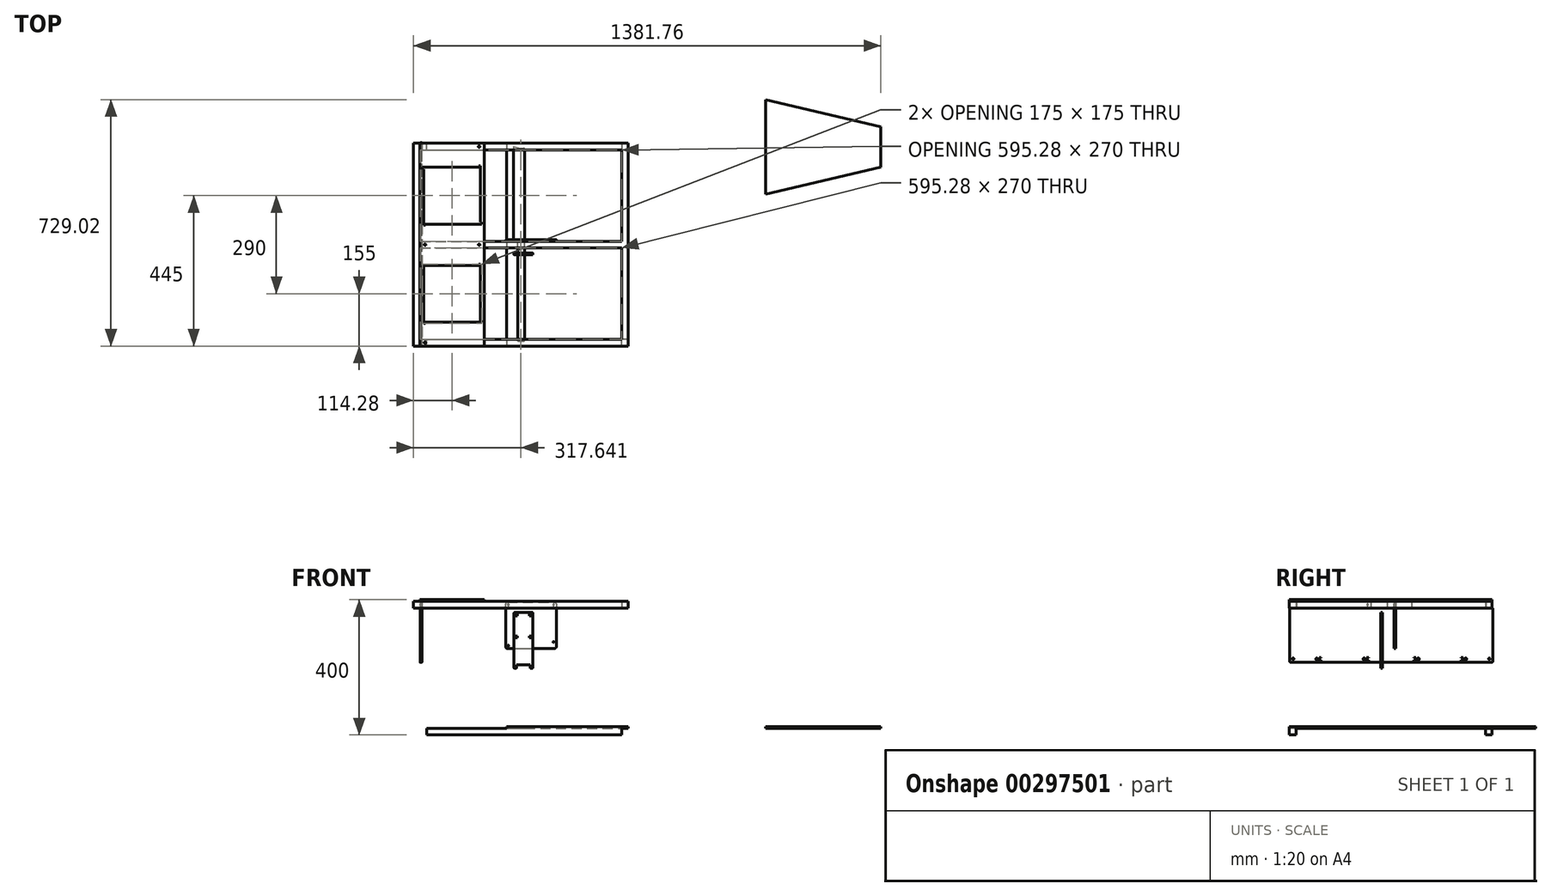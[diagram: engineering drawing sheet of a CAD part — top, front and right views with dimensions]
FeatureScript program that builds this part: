
annotation { "Feature Type Name" : "Feature", "Feature Type Description" : "" }
export const myFeature = defineFeature(function(context is Context, id is Id, definition is map)
    precondition{}
    {
        {
            var Q0;
            Q0=qCreatedBy(makeId("Front.planeOp"),FACE);
            var sketch = newSketch(context, id + "F0", { "sketchPlane" : qUnion([Q0])});
            skLineSegment(sketch, "E0", {"start": v(-53, 64) * mm, "end": v(-53, 191) * mm});
            skCircle(sketch, "E1", {"center": v(-45, 67) * mm, "radius": 1.4 * mm});
            skCircle(sketch, "E2", {"center": v(89, 78) * mm, "radius": 1.4 * mm});
            skLineSegment(sketch, "E3", {"start": v(97, 191) * mm, "end": v(97, 64) * mm});
            skLineSegment(sketch, "E4", {"start": v(-48, 196) * mm, "end": v(92, 196) * mm});
            skArc(sketch, "E5.filletArc", {"start": v(-48, 196) * mm, "mid": v(-51.54, 194.54) * mm, "end": v(-53, 191) * mm});
            skArc(sketch, "E6.filletArc", {"start": v(97, 191) * mm, "mid": v(95.54, 194.54) * mm, "end": v(92, 196) * mm});
            skCircle(sketch, "E7", {"center": v(-45, 188) * mm, "radius": 2.25 * mm});
            skCircle(sketch, "E8", {"center": v(89, 188) * mm, "radius": 2.25 * mm});
            skLineSegment(sketch, "E9", {"start": v(-48, 59) * mm, "end": v(92, 59) * mm});
            skArc(sketch, "E10.filletArc", {"start": v(-53, 64) * mm, "mid": v(-51.54, 60.46) * mm, "end": v(-48, 59) * mm});
            skArc(sketch, "E11.filletArc", {"start": v(92, 59) * mm, "mid": v(95.54, 60.46) * mm, "end": v(97, 64) * mm});
            skPoint(sketch, "E12", {"position": v(0, 0) * mm});
            skLineSegment(sketch, "E13.bottom", {"start": v(-23.05, 160.05) * mm, "end": v(-17.95, 160.05) * mm});
            skLineSegment(sketch, "E13.top", {"start": v(-23.05, 154.95) * mm, "end": v(-17.95, 154.95) * mm});
            skLineSegment(sketch, "E13.left", {"start": v(-23.05, 160.05) * mm, "end": v(-23.05, 154.95) * mm});
            skLineSegment(sketch, "E13.right", {"start": v(-17.95, 160.05) * mm, "end": v(-17.95, 154.95) * mm});
            skLineSegment(sketch, "E14.bottom", {"start": v(17.95, 160.05) * mm, "end": v(23.05, 160.05) * mm});
            skLineSegment(sketch, "E14.top", {"start": v(17.95, 154.95) * mm, "end": v(23.05, 154.95) * mm});
            skLineSegment(sketch, "E14.left", {"start": v(17.95, 160.05) * mm, "end": v(17.95, 154.95) * mm});
            skLineSegment(sketch, "E14.right", {"start": v(23.05, 160.05) * mm, "end": v(23.05, 154.95) * mm});
            skLineSegment(sketch, "E15.bottom", {"start": v(-23.05, 95.05) * mm, "end": v(-17.95, 95.05) * mm});
            skLineSegment(sketch, "E15.top", {"start": v(-23.05, 89.95) * mm, "end": v(-17.95, 89.95) * mm});
            skLineSegment(sketch, "E15.left", {"start": v(-23.05, 95.05) * mm, "end": v(-23.05, 89.95) * mm});
            skLineSegment(sketch, "E15.right", {"start": v(-17.95, 95.05) * mm, "end": v(-17.95, 89.95) * mm});
            skLineSegment(sketch, "E16.bottom", {"start": v(23.05, 95.05) * mm, "end": v(17.95, 95.05) * mm});
            skLineSegment(sketch, "E16.top", {"start": v(23.05, 89.95) * mm, "end": v(17.95, 89.95) * mm});
            skLineSegment(sketch, "E16.left", {"start": v(23.05, 95.05) * mm, "end": v(23.05, 89.95) * mm});
            skLineSegment(sketch, "E16.right", {"start": v(17.95, 95.05) * mm, "end": v(17.95, 89.95) * mm});
            skPoint(sketch, "E17", {"position": v(-20.5, 160.05) * mm});
            skPoint(sketch, "E18", {"position": v(20.5, 160.05) * mm});
            skPoint(sketch, "E19", {"position": v(23.05, 157.5) * mm});
            skPoint(sketch, "E20", {"position": v(-23.05, 157.5) * mm});
            skPoint(sketch, "E21", {"position": v(-23.05, 92.5) * mm});
            skPoint(sketch, "E22", {"position": v(17.95, 92.5) * mm});
            skPoint(sketch, "E23.middle.positionSnap0", {"position": v(23.05, 92.5) * mm});
            skPoint(sketch, "E23.centerSnap0", {"position": v(23.05, 92.5) * mm});
            skPoint(sketch, "E24", {"position": v(60.49, 176) * mm});
            skSolve(sketch);
        }
        {
            var Q0;
            Q0=qCreatedBy(makeId("Front.planeOp"),FACE);
            cPlane(context, id + "F1", {"entities" : qUnion([Q0]), "cplaneType" : CPlaneType.OFFSET, "offset" : (17 + 18) * mm, "width" : 150 * mm, "height" : 150 * mm});
        }
        {
            var Q0;
            Q0=qCreatedBy(id+"F1.planeOp",FACE);
            var sketch = newSketch(context, id + "F2", { "sketchPlane" : qUnion([Q0])});
            skPoint(sketch, "E25", {"position": v(0, 0) * mm});
            skCircle(sketch, "E26", {"center": v(-24, 5) * mm, "radius": 1.4 * mm});
            skCircle(sketch, "E27", {"center": v(24, 5) * mm, "radius": 1.4 * mm});
            skLineSegment(sketch, "E28", {"start": v(-26, 0) * mm, "end": v(-22, 0) * mm});
            skLineSegment(sketch, "E29.trimOffspring", {"start": v(22, 0) * mm, "end": v(26, 0) * mm});
            skLineSegment(sketch, "E30.top", {"start": v(-20, 11) * mm, "end": v(20, 11) * mm});
            skLineSegment(sketch, "E30.left", {"start": v(-20, 2) * mm, "end": v(-20, 11) * mm});
            skLineSegment(sketch, "E30.right", {"start": v(20, 2) * mm, "end": v(20, 11) * mm});
            skPoint(sketch, "E30.middle", {"position": v(0, 5.5) * mm});
            skLineSegment(sketch, "E31", {"start": v(-28, 2) * mm, "end": v(-28, 163) * mm});
            skLineSegment(sketch, "E32", {"start": v(-26, 165) * mm, "end": v(26, 165) * mm});
            skLineSegment(sketch, "E33", {"start": v(28, 163) * mm, "end": v(28, 2) * mm});
            skLineSegment(sketch, "E34.bottom", {"start": v(-23.05, 160.05) * mm, "end": v(-17.95, 160.05) * mm});
            skLineSegment(sketch, "E34.top", {"start": v(-23.05, 154.95) * mm, "end": v(-17.95, 154.95) * mm});
            skLineSegment(sketch, "E34.left", {"start": v(-23.05, 160.05) * mm, "end": v(-23.05, 154.95) * mm});
            skLineSegment(sketch, "E34.right", {"start": v(-17.95, 160.05) * mm, "end": v(-17.95, 154.95) * mm});
            skLineSegment(sketch, "E35.bottom", {"start": v(17.95, 160.05) * mm, "end": v(23.05, 160.05) * mm});
            skLineSegment(sketch, "E35.top", {"start": v(17.95, 154.95) * mm, "end": v(23.05, 154.95) * mm});
            skLineSegment(sketch, "E35.left", {"start": v(17.95, 160.05) * mm, "end": v(17.95, 154.95) * mm});
            skLineSegment(sketch, "E35.right", {"start": v(23.05, 160.05) * mm, "end": v(23.05, 154.95) * mm});
            skLineSegment(sketch, "E36.bottom", {"start": v(-23.05, 95.05) * mm, "end": v(-17.95, 95.05) * mm});
            skLineSegment(sketch, "E36.top", {"start": v(-23.05, 89.95) * mm, "end": v(-17.95, 89.95) * mm});
            skLineSegment(sketch, "E36.left", {"start": v(-23.05, 95.05) * mm, "end": v(-23.05, 89.95) * mm});
            skLineSegment(sketch, "E36.right", {"start": v(-17.95, 95.05) * mm, "end": v(-17.95, 89.95) * mm});
            skLineSegment(sketch, "E37.bottom", {"start": v(23.05, 95.05) * mm, "end": v(17.95, 95.05) * mm});
            skLineSegment(sketch, "E37.top", {"start": v(23.05, 89.95) * mm, "end": v(17.95, 89.95) * mm});
            skLineSegment(sketch, "E37.left", {"start": v(23.05, 95.05) * mm, "end": v(23.05, 89.95) * mm});
            skLineSegment(sketch, "E37.right", {"start": v(17.95, 95.05) * mm, "end": v(17.95, 89.95) * mm});
            skPoint(sketch, "E38.visualSharp", {"position": v(-28, 0) * mm});
            skArc(sketch, "E38.filletArc", {"start": v(-28, 2) * mm, "mid": v(-27.41, 0.59) * mm, "end": v(-26, 0) * mm});
            skPoint(sketch, "E39.visualSharp", {"position": v(-20, 0) * mm});
            skArc(sketch, "E39.filletArc", {"start": v(-22, 0) * mm, "mid": v(-20.59, 0.59) * mm, "end": v(-20, 2) * mm});
            skPoint(sketch, "E40.visualSharp", {"position": v(20, 0) * mm});
            skArc(sketch, "E40.filletArc", {"start": v(20, 2) * mm, "mid": v(20.59, 0.59) * mm, "end": v(22, 0) * mm});
            skPoint(sketch, "E41.visualSharp", {"position": v(28, 0) * mm});
            skArc(sketch, "E41.filletArc", {"start": v(26, 0) * mm, "mid": v(27.41, 0.59) * mm, "end": v(28, 2) * mm});
            skPoint(sketch, "E42.visualSharp", {"position": v(-28, 165) * mm});
            skArc(sketch, "E42.filletArc", {"start": v(-26, 165) * mm, "mid": v(-27.41, 164.41) * mm, "end": v(-28, 163) * mm});
            skPoint(sketch, "E43.visualSharp", {"position": v(28, 165) * mm});
            skArc(sketch, "E43.filletArc", {"start": v(28, 163) * mm, "mid": v(27.41, 164.41) * mm, "end": v(26, 165) * mm});
            skPoint(sketch, "E44", {"position": v(-20.5, 160.05) * mm});
            skPoint(sketch, "E45", {"position": v(20.5, 160.05) * mm});
            skPoint(sketch, "E46", {"position": v(23.05, 157.5) * mm});
            skPoint(sketch, "E47", {"position": v(-23.05, 157.5) * mm});
            skPoint(sketch, "E48", {"position": v(-23.05, 92.5) * mm});
            skPoint(sketch, "E49", {"position": v(17.95, 92.5) * mm});
            skLineSegment(sketch, "E50", {"start": v(38, 165) * mm, "end": v(38, 160) * mm});
            skLineSegment(sketch, "E51.bottom", {"start": v(38, 155) * mm, "end": v(33, 155) * mm});
            skLineSegment(sketch, "E51.top", {"start": v(38, 160) * mm, "end": v(33, 160) * mm});
            skLineSegment(sketch, "E51.right", {"start": v(33, 155) * mm, "end": v(33, 160) * mm});
            skPoint(sketch, "E51.middle", {"position": v(35.5, 157.5) * mm});
            skLineSegment(sketch, "E52.bottom", {"start": v(38, 90) * mm, "end": v(33, 90) * mm});
            skLineSegment(sketch, "E52.top", {"start": v(38, 95) * mm, "end": v(33, 95) * mm});
            skLineSegment(sketch, "E52.right", {"start": v(33, 90) * mm, "end": v(33, 95) * mm});
            skPoint(sketch, "E52.middle", {"position": v(35.5, 92.5) * mm});
            skPoint(sketch, "E52.middle.positionSnap0", {"position": v(23.05, 92.5) * mm});
            skPoint(sketch, "E52.centerSnap0", {"position": v(23.05, 92.5) * mm});
            skLineSegment(sketch, "E53.bottom", {"start": v(-40, 160) * mm, "end": v(-35, 160) * mm});
            skLineSegment(sketch, "E53.top", {"start": v(-40, 155) * mm, "end": v(-35, 155) * mm});
            skLineSegment(sketch, "E53.right", {"start": v(-35, 160) * mm, "end": v(-35, 155) * mm});
            skPoint(sketch, "E53.middle", {"position": v(-37.5, 157.5) * mm});
            skLineSegment(sketch, "E54.bottom", {"start": v(-40, 95) * mm, "end": v(-35, 95) * mm});
            skLineSegment(sketch, "E54.top", {"start": v(-40, 90) * mm, "end": v(-35, 90) * mm});
            skLineSegment(sketch, "E54.right", {"start": v(-35, 95) * mm, "end": v(-35, 90) * mm});
            skPoint(sketch, "E54.middle", {"position": v(-37.5, 92.5) * mm});
            skLineSegment(sketch, "E55.trimOffspring", {"start": v(38, 155) * mm, "end": v(38, 95) * mm});
            skLineSegment(sketch, "E56.trimOffspring", {"start": v(38, 90) * mm, "end": v(38, 85) * mm});
            skLineSegment(sketch, "E57", {"start": v(38, 165) * mm, "end": v(59, 165) * mm});
            skLineSegment(sketch, "E58", {"start": v(59, 165) * mm, "end": v(59, 160) * mm});
            skLineSegment(sketch, "E59", {"start": v(59, 160) * mm, "end": v(64, 160) * mm});
            skLineSegment(sketch, "E60", {"start": v(64, 160) * mm, "end": v(64, 155) * mm});
            skLineSegment(sketch, "E61", {"start": v(64, 155) * mm, "end": v(59, 155) * mm});
            skLineSegment(sketch, "E62", {"start": v(59, 155) * mm, "end": v(59, 95) * mm});
            skLineSegment(sketch, "E63", {"start": v(59, 95) * mm, "end": v(64, 95) * mm});
            skLineSegment(sketch, "E64", {"start": v(64, 95) * mm, "end": v(64, 90) * mm});
            skLineSegment(sketch, "E65", {"start": v(64, 90) * mm, "end": v(59, 90) * mm});
            skLineSegment(sketch, "E66", {"start": v(59, 90) * mm, "end": v(59, 85) * mm});
            skLineSegment(sketch, "E67", {"start": v(59, 85) * mm, "end": v(38, 85) * mm});
            skLineSegment(sketch, "E68.trimOffspring", {"start": v(-40, 155) * mm, "end": v(-40, 95) * mm});
            skPoint(sketch, "E69.start.orphan", {"position": v(-40, 165) * mm});
            skLineSegment(sketch, "E70.trimOffspring", {"start": v(-40, 90) * mm, "end": v(-40, 85) * mm});
            skLineSegment(sketch, "E71", {"start": v(-40, 160) * mm, "end": v(-40, 165) * mm});
            skLineSegment(sketch, "E72", {"start": v(-40, 165) * mm, "end": v(-61, 165) * mm});
            skLineSegment(sketch, "E73", {"start": v(-61, 165) * mm, "end": v(-61, 160) * mm});
            skLineSegment(sketch, "E74", {"start": v(-61, 160) * mm, "end": v(-66, 160) * mm});
            skLineSegment(sketch, "E75", {"start": v(-66, 160) * mm, "end": v(-66, 155) * mm});
            skPoint(sketch, "E75.endSnap0", {"position": v(-37.5, 155) * mm});
            skLineSegment(sketch, "E76", {"start": v(-66, 155) * mm, "end": v(-61, 155) * mm});
            skLineSegment(sketch, "E77", {"start": v(-61, 155) * mm, "end": v(-61, 95) * mm});
            skLineSegment(sketch, "E78", {"start": v(-61, 95) * mm, "end": v(-66, 95) * mm});
            skLineSegment(sketch, "E79", {"start": v(-66, 95) * mm, "end": v(-66, 90) * mm});
            skLineSegment(sketch, "E80", {"start": v(-66, 90) * mm, "end": v(-61, 90) * mm});
            skLineSegment(sketch, "E81", {"start": v(-61, 90) * mm, "end": v(-61, 85) * mm});
            skLineSegment(sketch, "E82", {"start": v(-61, 85) * mm, "end": v(-40, 85) * mm});
            skSolve(sketch);
        }
        {
            var Q0;
            Q0=makeQuery(id+"F2.imprint","IMPRINT",FACE,{"disambiguationData":[TD([[makeQuery(id+"F2.imprint","IMPRINT",EDGE,{"derivedFrom":sQuery(id+"F2.wireOp",EDGE,"E26")}),-1.0]])]});
            extrude(context, id + "F3", {"entities" : qUnion([Q0]), "depth" : 5 * mm});
        }
        {
            var Q0;
            Q0=makeQuery(id+"F0.imprint","IMPRINT",FACE,{"disambiguationData":[TD([[makeQuery(id+"F0.imprint","IMPRINT",EDGE,{"derivedFrom":sQuery(id+"F0.wireOp",EDGE,"E0")}),-1.0]])]});
            extrude(context, id + "F4", {"entities" : qUnion([Q0]), "oppositeDirection" : true, "depth" : 5 * mm});
        }
        {
            var Q0;
            Q0=qCreatedBy(id+"F1.planeOp",FACE);
            var sketch = newSketch(context, id + "F5", { "sketchPlane" : qUnion([Q0])});
            skPoint(sketch, "E83", {"position": v(-11.66, -156.67) * mm});
            skPoint(sketch, "E84", {"position": v(-265.28, 29.4) * mm});
            skPoint(sketch, "E85", {"position": v(168.31, 153.68) * mm});
            skLineSegment(sketch, "E86.bottom", {"start": v(-17.16, -156.67) * mm, "end": v(3.84, -156.67) * mm});
            skLineSegment(sketch, "E86.top", {"start": v(-17.16, -151.67) * mm, "end": v(3.84, -151.67) * mm});
            skLineSegment(sketch, "E86.left", {"start": v(-17.16, -156.67) * mm, "end": v(-17.16, -151.67) * mm});
            skLineSegment(sketch, "E86.right", {"start": v(3.84, -156.67) * mm, "end": v(3.84, -151.67) * mm});
            skCircle(sketch, "E87", {"center": v(168.31, 153.68) * mm, "radius": 6 * mm});
            skSolve(sketch);
        }
        {
            var Q0;
            Q0=qCreatedBy(makeId("Top.planeOp"),FACE);
            cPlane(context, id + "F6", {"entities" : qUnion([Q0]), "cplaneType" : CPlaneType.OFFSET, "offset" : 172 * mm, "oppositeDirection" : true, "width" : 150 * mm, "height" : 150 * mm});
        }
        {
            var Q0;
            Q0=qCreatedBy(id+"F6.planeOp",FACE);
            var sketch = newSketch(context, id + "F7", { "sketchPlane" : qUnion([Q0])});
            skLineSegment(sketch, "E88.top", {"start": v(290, 290) * mm, "end": v(-50, 290) * mm});
            skLineSegment(sketch, "E89.top", {"start": v(290, -310) * mm, "end": v(-50, -310) * mm});
            skLineSegment(sketch, "E90", {"start": v(-50, 290) * mm, "end": v(-50, -310) * mm});
            skLineSegment(sketch, "E91", {"start": v(310, 269.5) * mm, "end": v(310, -289.5) * mm});
            skPoint(sketch, "E92", {"position": v(310, -10) * mm});
            skLineSegment(sketch, "E93.top", {"start": v(310, 269.5) * mm, "end": v(290, 269.5) * mm});
            skLineSegment(sketch, "E93.right", {"start": v(290, 290) * mm, "end": v(290, 269.5) * mm});
            skPoint(sketch, "E93.left.start.orphan", {"position": v(310, 290) * mm});
            skLineSegment(sketch, "E94.top", {"start": v(310, -289.5) * mm, "end": v(290, -289.5) * mm});
            skLineSegment(sketch, "E94.right", {"start": v(290, -310) * mm, "end": v(290, -289.5) * mm});
            skPoint(sketch, "E94.left.start.orphan", {"position": v(310, -310) * mm});
            skLineSegment(sketch, "E95", {"start": v(-30, 280) * mm, "end": v(-30, 0) * mm});
            skLineSegment(sketch, "E96", {"start": v(310, 200) * mm, "end": v(310, 80) * mm});
            skLineSegment(sketch, "E97", {"start": v(-30, 280) * mm, "end": v(310, 200) * mm});
            skLineSegment(sketch, "E98", {"start": v(-30, 0) * mm, "end": v(310, 80) * mm});
            skPoint(sketch, "E99.middle", {"position": v(-11.66, -35) * mm});
            skLineSegment(sketch, "E100", {"start": v(-17.16, -54.99) * mm, "end": v(-17.16, 17.36) * mm});
            skLineSegment(sketch, "E101", {"start": v(3.84, 16.76) * mm, "end": v(3.84, -54.7) * mm});
            skPoint(sketch, "E102", {"position": v(-50, -10) * mm});
            skPoint(sketch, "E103", {"position": v(-17.16, -10) * mm});
            skCircle(sketch, "E104", {"center": v(-4.16, -230) * mm, "radius": 3 * mm});
            skPoint(sketch, "E105", {"position": v(-4.16, -10) * mm});
            skLineSegment(sketch, "E106.bottom", {"start": v(3.84, -292) * mm, "end": v(3.84, 272) * mm});
            skPoint(sketch, "E107", {"position": v(-4.16, -90) * mm});
            skPoint(sketch, "E108", {"position": v(-4.16, -35) * mm});
            skPoint(sketch, "E109", {"position": v(-4.16, -285) * mm});
            skPoint(sketch, "E110", {"position": v(-4.16, -160) * mm});
            skCircle(sketch, "E111", {"center": v(-4.16, -285) * mm, "radius": 3 * mm});
            skLineSegment(sketch, "E112.bottom", {"start": v(-11.16, -278) * mm, "end": v(-11.16, -272) * mm});
            skLineSegment(sketch, "E112.top", {"start": v(-9.16, -278) * mm, "end": v(-9.16, -272) * mm});
            skLineSegment(sketch, "E112.left", {"start": v(-11.16, -278) * mm, "end": v(-9.16, -278) * mm});
            skLineSegment(sketch, "E112.right", {"start": v(-11.16, -272) * mm, "end": v(-9.16, -272) * mm});
            skCircle(sketch, "E113", {"center": v(-4.16, -90) * mm, "radius": 3 * mm});
            skCircle(sketch, "E114", {"center": v(-4.16, -35) * mm, "radius": 3 * mm});
            skLineSegment(sketch, "E115", {"start": v(-17.16, -295) * mm, "end": v(0.84, -295) * mm});
            skPoint(sketch, "E116", {"position": v(-4.16, 70) * mm});
            skPoint(sketch, "E117", {"position": v(-4.16, 210) * mm});
            skPoint(sketch, "E118", {"position": v(-4.16, 265) * mm});
            skPoint(sketch, "E119", {"position": v(-4.16, 15) * mm});
            skPoint(sketch, "E120", {"position": v(-4.16, 140) * mm});
            skCircle(sketch, "E121", {"center": v(-4.16, 15) * mm, "radius": 3 * mm});
            skLineSegment(sketch, "E122.bottom", {"start": v(-11.16, -223) * mm, "end": v(-11.16, -217) * mm});
            skLineSegment(sketch, "E122.top", {"start": v(-9.16, -223) * mm, "end": v(-9.16, -217) * mm});
            skLineSegment(sketch, "E122.left", {"start": v(-11.16, -223) * mm, "end": v(-9.16, -223) * mm});
            skLineSegment(sketch, "E122.right", {"start": v(-11.16, -217) * mm, "end": v(-9.16, -217) * mm});
            skLineSegment(sketch, "E123.bottom", {"start": v(-11.16, -83) * mm, "end": v(-11.16, -77) * mm});
            skLineSegment(sketch, "E123.top", {"start": v(-9.16, -83) * mm, "end": v(-9.16, -77) * mm});
            skLineSegment(sketch, "E123.left", {"start": v(-11.16, -83) * mm, "end": v(-9.16, -83) * mm});
            skLineSegment(sketch, "E123.right", {"start": v(-11.16, -77) * mm, "end": v(-9.16, -77) * mm});
            skLineSegment(sketch, "E124.bottom", {"start": v(-11.16, 57) * mm, "end": v(-11.16, 63) * mm});
            skLineSegment(sketch, "E124.top", {"start": v(-9.16, 57) * mm, "end": v(-9.16, 63) * mm});
            skLineSegment(sketch, "E124.left", {"start": v(-11.16, 57) * mm, "end": v(-9.16, 57) * mm});
            skLineSegment(sketch, "E124.right", {"start": v(-11.16, 63) * mm, "end": v(-9.16, 63) * mm});
            skCircle(sketch, "E125", {"center": v(-4.16, 70) * mm, "radius": 3 * mm});
            skLineSegment(sketch, "E126.bottom", {"start": v(-11.16, 197) * mm, "end": v(-11.16, 203) * mm});
            skLineSegment(sketch, "E126.top", {"start": v(-9.16, 197) * mm, "end": v(-9.16, 203) * mm});
            skLineSegment(sketch, "E126.left", {"start": v(-11.16, 197) * mm, "end": v(-9.16, 197) * mm});
            skLineSegment(sketch, "E126.right", {"start": v(-11.16, 203) * mm, "end": v(-9.16, 203) * mm});
            skCircle(sketch, "E127", {"center": v(-4.16, 210) * mm, "radius": 3 * mm});
            skLineSegment(sketch, "E128.bottom", {"start": v(-11.16, 252) * mm, "end": v(-11.16, 258) * mm});
            skLineSegment(sketch, "E128.top", {"start": v(-9.16, 252) * mm, "end": v(-9.16, 258) * mm});
            skLineSegment(sketch, "E128.left", {"start": v(-11.16, 252) * mm, "end": v(-9.16, 252) * mm});
            skLineSegment(sketch, "E128.right", {"start": v(-11.16, 258) * mm, "end": v(-9.16, 258) * mm});
            skCircle(sketch, "E129", {"center": v(-4.16, 265) * mm, "radius": 3 * mm});
            skLineSegment(sketch, "E130", {"start": v(-17.16, 275) * mm, "end": v(0.84, 275) * mm});
            skLineSegment(sketch, "E131.bottom", {"start": v(-11.16, 22) * mm, "end": v(-11.16, 28) * mm});
            skLineSegment(sketch, "E131.top", {"start": v(-9.16, 22) * mm, "end": v(-9.16, 28) * mm});
            skLineSegment(sketch, "E131.left", {"start": v(-11.16, 22) * mm, "end": v(-9.16, 22) * mm});
            skLineSegment(sketch, "E131.right", {"start": v(-11.16, 28) * mm, "end": v(-9.16, 28) * mm});
            skLineSegment(sketch, "E132.bottom", {"start": v(-11.16, -48) * mm, "end": v(-11.16, -42) * mm});
            skLineSegment(sketch, "E132.top", {"start": v(-9.16, -48) * mm, "end": v(-9.16, -42) * mm});
            skLineSegment(sketch, "E132.left", {"start": v(-11.16, -48) * mm, "end": v(-9.16, -48) * mm});
            skLineSegment(sketch, "E132.right", {"start": v(-11.16, -42) * mm, "end": v(-9.16, -42) * mm});
            skLineSegment(sketch, "E133", {"start": v(-17.16, -295) * mm, "end": v(-17.16, 275) * mm});
            skLineSegment(sketch, "E134.top", {"start": v(-12.16, -295) * mm, "end": v(-12.16, 275) * mm});
            skLineSegment(sketch, "E134.left", {"start": v(-17.16, -295) * mm, "end": v(-12.16, -295) * mm});
            skLineSegment(sketch, "E134.right", {"start": v(-17.16, 275) * mm, "end": v(-12.16, 275) * mm});
            skLineSegment(sketch, "E135.bottom", {"start": v(0.89, -7.45) * mm, "end": v(0.89, -12.55) * mm});
            skLineSegment(sketch, "E135.top", {"start": v(-9.21, -7.45) * mm, "end": v(-9.21, -12.55) * mm});
            skLineSegment(sketch, "E135.left", {"start": v(0.89, -7.45) * mm, "end": v(-9.21, -7.45) * mm});
            skLineSegment(sketch, "E135.right", {"start": v(0.89, -12.55) * mm, "end": v(-9.21, -12.55) * mm});
            skPoint(sketch, "E136.visualSharp", {"position": v(3.84, -295) * mm});
            skArc(sketch, "E136.filletArc", {"start": v(0.84, -295) * mm, "mid": v(2.96, -294.12) * mm, "end": v(3.84, -292) * mm});
            skPoint(sketch, "E137.visualSharp", {"position": v(3.84, 275) * mm});
            skArc(sketch, "E137.filletArc", {"start": v(3.84, 272) * mm, "mid": v(2.96, 274.12) * mm, "end": v(0.84, 275) * mm});
            skLineSegment(sketch, "E138", {"start": v(716.48, 419.02) * mm, "end": v(716.48, 139.02) * mm});
            skLineSegment(sketch, "E139", {"start": v(1056.48, 339.02) * mm, "end": v(1056.48, 219.02) * mm});
            skLineSegment(sketch, "E140", {"start": v(716.48, 419.02) * mm, "end": v(1056.48, 339.02) * mm});
            skLineSegment(sketch, "E141", {"start": v(716.48, 139.02) * mm, "end": v(1056.48, 219.02) * mm});
            skSolve(sketch);
        }
        {
            var Q0;
            Q0=qCreatedBy(makeId("Top.planeOp"),FACE);
            cPlane(context, id + "F8", {"entities" : qUnion([Q0]), "cplaneType" : CPlaneType.OFFSET, "offset" : 178 * mm, "width" : 150 * mm, "height" : 150 * mm});
        }
        {
            var Q0;
            Q0=qCreatedBy(id+"F8.planeOp",FACE);
            var sketch = newSketch(context, id + "F9", { "sketchPlane" : qUnion([Q0])});
            skLineSegment(sketch, "E142.bottom", {"start": v(-305.28, 270) * mm, "end": v(290, 270) * mm});
            skLineSegment(sketch, "E142.top", {"start": v(-305.28, -290) * mm, "end": v(290, -290) * mm});
            skLineSegment(sketch, "E142.left", {"start": v(-305.28, 270) * mm, "end": v(-305.28, -290) * mm});
            skLineSegment(sketch, "E142.right", {"start": v(290, 270) * mm, "end": v(290, -290) * mm});
            skLineSegment(sketch, "E143.bottom", {"start": v(-325.28, 290) * mm, "end": v(310, 290) * mm});
            skLineSegment(sketch, "E143.top", {"start": v(-325.28, -310) * mm, "end": v(310, -310) * mm});
            skLineSegment(sketch, "E143.left", {"start": v(-325.28, 290) * mm, "end": v(-325.28, -310) * mm});
            skLineSegment(sketch, "E143.right", {"start": v(310, 290) * mm, "end": v(310, -310) * mm});
            skLineSegment(sketch, "E144", {"start": v(-305.28, 0) * mm, "end": v(290, 0) * mm});
            skLineSegment(sketch, "E145", {"start": v(-305.28, -20) * mm, "end": v(290, -20) * mm});
            skLineSegment(sketch, "E146.bottom", {"start": v(-305.28, 270) * mm, "end": v(-325.28, 270) * mm});
            skLineSegment(sketch, "E146.top", {"start": v(-305.28, 290) * mm, "end": v(-325.28, 290) * mm});
            skLineSegment(sketch, "E146.left", {"start": v(-305.28, 270) * mm, "end": v(-305.28, 290) * mm});
            skLineSegment(sketch, "E146.right", {"start": v(-325.28, 270) * mm, "end": v(-325.28, 290) * mm});
            skLineSegment(sketch, "E147.bottom", {"start": v(-305.28, -290) * mm, "end": v(-325.28, -290) * mm});
            skLineSegment(sketch, "E147.top", {"start": v(-305.28, -310) * mm, "end": v(-325.28, -310) * mm});
            skLineSegment(sketch, "E147.left", {"start": v(-305.28, -290) * mm, "end": v(-305.28, -310) * mm});
            skLineSegment(sketch, "E147.right", {"start": v(-325.28, -290) * mm, "end": v(-325.28, -310) * mm});
            skLineSegment(sketch, "E148.bottom", {"start": v(310, -310) * mm, "end": v(290, -310) * mm});
            skLineSegment(sketch, "E148.top", {"start": v(310, -290) * mm, "end": v(290, -290) * mm});
            skLineSegment(sketch, "E148.left", {"start": v(310, -310) * mm, "end": v(310, -290) * mm});
            skLineSegment(sketch, "E148.right", {"start": v(290, -310) * mm, "end": v(290, -290) * mm});
            skLineSegment(sketch, "E149.bottom", {"start": v(310, 290) * mm, "end": v(290, 290) * mm});
            skLineSegment(sketch, "E149.top", {"start": v(310, 270) * mm, "end": v(290, 270) * mm});
            skLineSegment(sketch, "E149.left", {"start": v(310, 290) * mm, "end": v(310, 270) * mm});
            skLineSegment(sketch, "E149.right", {"start": v(290, 290) * mm, "end": v(290, 270) * mm});
            skPoint(sketch, "E150", {"position": v(-300.28, -35) * mm});
            skPoint(sketch, "E151", {"position": v(-305.28, -35) * mm});
            skSolve(sketch);
        }
        {
            var Q0;
            Q0 = qSketchRegion(id + "F9", true);
            var Q1;
            {var subQ0=sQuery(id+"F9.wireOp",EDGE,"E144");Q1=makeQuery(id+"F9.imprint","IMPRINT",FACE,{"disambiguationData":[TD([[makeQuery(id+"F9.imprint","IMPRINT",EDGE,{"derivedFrom":subQ0}),-1.0]])]});}
            extrude(context, id + "F10", {"entities" : qUnion([Q0, Q1]), "operationType" : NewBodyOperationType.ADD, "depth" : 20 * mm});
        }
        {
            var Q0;
            Q0 = qSketchRegion(id + "F7", true);
            extrude(context, id + "F11", {"entities" : qUnion([Q0]), "operationType" : NewBodyOperationType.ADD, "oppositeDirection" : true, "depth" : 5 * mm});
        }
        {
            var Q0;
            Q0=sQuery(id+"F9.wireOp",EDGE,"E147.bottom");
            var Q1;
            Q1=sQuery(id+"F9.wireOp",EDGE,"E147.left");
            var Q2;
            Q2=sQuery(id+"F9.wireOp",EDGE,"E147.top");
            var Q3;
            Q3=sQuery(id+"F9.wireOp",EDGE,"E147.right");
            var Q4;
            Q4=sQuery(id+"F9.wireOp",EDGE,"E148.top");
            var Q5;
            Q5=sQuery(id+"F9.wireOp",EDGE,"E148.left");
            var Q6;
            Q6=sQuery(id+"F9.wireOp",EDGE,"E148.bottom");
            var Q7;
            Q7=sQuery(id+"F9.wireOp",EDGE,"E148.right");
            var Q8;
            Q8=sQuery(id+"F9.wireOp",EDGE,"E149.right");
            var Q9;
            Q9=sQuery(id+"F9.wireOp",EDGE,"E149.left");
            var Q10;
            Q10=sQuery(id+"F9.wireOp",EDGE,"E149.bottom");
            var Q11;
            Q11=sQuery(id+"F9.wireOp",EDGE,"E149.top");
            var Q12;
            Q12=sQuery(id+"F9.wireOp",EDGE,"E146.bottom");
            var Q13;
            Q13=sQuery(id+"F9.wireOp",EDGE,"E146.top");
            var Q14;
            Q14=sQuery(id+"F9.wireOp",EDGE,"E146.right");
            var Q15;
            Q15=sQuery(id+"F9.wireOp",EDGE,"E146.left");
            extrude(context, id + "F12", {"bodyType" : ToolBodyType.SURFACE, "surfaceEntities" : qUnion([Q0, Q1, Q2, Q3, Q4, Q5, Q6, Q7, Q8, Q9, Q10, Q11, Q12, Q13, Q14, Q15]), "oppositeDirection" : true, "depth" : 500 * mm});
        }
        {
            var Q0;
            Q0=makeQuery(id+"F12.opExtrude","SWEPT_FACE",FACE,{"disambiguationData":[OSD([sQuery(id+"F9.wireOp",EDGE,"E148.right")])]});
            var sketch = newSketch(context, id + "F13", { "sketchPlane" : qUnion([Q0])});
            skLineSegment(sketch, "E152.bottom", {"start": v(-310, -177) * mm, "end": v(-290, -177) * mm});
            skLineSegment(sketch, "E152.top", {"start": v(-310, -197) * mm, "end": v(-290, -197) * mm});
            skLineSegment(sketch, "E152.left", {"start": v(-310, -177) * mm, "end": v(-310, -197) * mm});
            skLineSegment(sketch, "E152.right", {"start": v(-290, -177) * mm, "end": v(-290, -197) * mm});
            skLineSegment(sketch, "E153.bottom", {"start": v(270, -177) * mm, "end": v(290, -177) * mm});
            skLineSegment(sketch, "E153.top", {"start": v(270, -197) * mm, "end": v(290, -197) * mm});
            skLineSegment(sketch, "E153.left", {"start": v(270, -177) * mm, "end": v(270, -197) * mm});
            skLineSegment(sketch, "E153.right", {"start": v(290, -177) * mm, "end": v(290, -197) * mm});
            skSolve(sketch);
        }
        {
            var Q0;
            Q0 = qSketchRegion(id + "F13", true);
            extrude(context, id + "F14", {"entities" : qUnion([Q0]), "operationType" : NewBodyOperationType.ADD, "oppositeDirection" : true, "depth" : 576 * mm});
        }
        {
            var Q0;
            {var subQ0=sQuery(id+"F9.wireOp",EDGE,"E142.left");Q0=makeQuery(id+"F10.opExtrude","SWEPT_FACE",FACE,{"disambiguationData":[OSD([subQ0]),TDD([makeQuery(id+"F9.imprint","IMPRINT",EDGE,{"disambiguationData":[TD([[makeQuery(id+"F9.imprint","INTERSECT",VERTEX,{"derivedFrom":[subQ0,sQuery(id+"F9.wireOp",EDGE,"E145")]}),-1.0]])],"derivedFrom":subQ0})])]});}
            var sketch = newSketch(context, id + "F15", { "sketchPlane" : qUnion([Q0])});
            skCircle(sketch, "E154", {"center": v(-228.5, 27.5) * mm, "radius": 3 * mm});
            skCircle(sketch, "E155.MirrorC", {"center": v(-88.5, 27.5) * mm, "radius": 3 * mm});
            skCircle(sketch, "E156", {"center": v(71.5, 27.5) * mm, "radius": 3 * mm});
            skCircle(sketch, "E157.MirrorC", {"center": v(211.5, 27.5) * mm, "radius": 3 * mm});
            skLineSegment(sketch, "E158.bottom", {"start": v(-306.5, 18) * mm, "end": v(289.5, 18) * mm});
            skLineSegment(sketch, "E158.left", {"start": v(-308.5, 20) * mm, "end": v(-308.5, 178) * mm});
            skLineSegment(sketch, "E158.right", {"start": v(291.5, 20) * mm, "end": v(291.5, 178) * mm});
            skPoint(sketch, "E159.visualSharp", {"position": v(-308.5, 18) * mm});
            skArc(sketch, "E159.filletArc", {"start": v(-308.5, 20) * mm, "mid": v(-307.91, 18.59) * mm, "end": v(-306.5, 18) * mm});
            skPoint(sketch, "E160.visualSharp", {"position": v(291.5, 18) * mm});
            skArc(sketch, "E160.filletArc", {"start": v(289.5, 18) * mm, "mid": v(290.91, 18.59) * mm, "end": v(291.5, 20) * mm});
            skLineSegment(sketch, "E161", {"start": v(-288, 198) * mm, "end": v(-68.5, 198) * mm});
            skLineSegment(sketch, "E162.top", {"start": v(-308.5, 178) * mm, "end": v(-288, 178) * mm});
            skLineSegment(sketch, "E162.right", {"start": v(-288, 198) * mm, "end": v(-288, 178) * mm});
            skLineSegment(sketch, "E163.top", {"start": v(291.5, 178) * mm, "end": v(271, 178) * mm});
            skLineSegment(sketch, "E163.right", {"start": v(271, 198) * mm, "end": v(271, 178) * mm});
            skLineSegment(sketch, "E164.top", {"start": v(51.5, 178) * mm, "end": v(-68.5, 178) * mm});
            skLineSegment(sketch, "E164.left", {"start": v(51.5, 198) * mm, "end": v(51.5, 178) * mm});
            skLineSegment(sketch, "E164.right", {"start": v(-68.5, 198) * mm, "end": v(-68.5, 178) * mm});
            skPoint(sketch, "E164.middle", {"position": v(-8.5, 188) * mm});
            skPoint(sketch, "E164.middle.positionSnap0", {"position": v(-8.5, 198) * mm});
            skPoint(sketch, "E164.centerSnap0", {"position": v(-8.5, 198) * mm});
            skPoint(sketch, "E165.orphan", {"position": v(-308.5, 198) * mm});
            skLineSegment(sketch, "E166.trimOffspring", {"start": v(51.5, 198) * mm, "end": v(271, 198) * mm});
            skPoint(sketch, "E167.orphan", {"position": v(291.5, 198) * mm});
            skCircle(sketch, "E168", {"center": v(-298.5, 28) * mm, "radius": 2.25 * mm});
            skCircle(sketch, "E169", {"center": v(281.5, 28) * mm, "radius": 2.25 * mm});
            skCircle(sketch, "E170", {"center": v(-78.5, 188) * mm, "radius": 2.25 * mm});
            skLineSegment(sketch, "E171.bottom", {"start": v(-221.5, 32.5) * mm, "end": v(-215.5, 32.5) * mm});
            skLineSegment(sketch, "E171.top", {"start": v(-221.5, 30.5) * mm, "end": v(-215.5, 30.5) * mm});
            skLineSegment(sketch, "E171.left", {"start": v(-221.5, 32.5) * mm, "end": v(-221.5, 30.5) * mm});
            skLineSegment(sketch, "E171.right", {"start": v(-215.5, 32.5) * mm, "end": v(-215.5, 30.5) * mm});
            skLineSegment(sketch, "E172.bottom", {"start": v(-221.5, 24.5) * mm, "end": v(-215.5, 24.5) * mm});
            skLineSegment(sketch, "E172.top", {"start": v(-221.5, 22.5) * mm, "end": v(-215.5, 22.5) * mm});
            skLineSegment(sketch, "E172.left", {"start": v(-221.5, 24.5) * mm, "end": v(-221.5, 22.5) * mm});
            skLineSegment(sketch, "E172.right", {"start": v(-215.5, 24.5) * mm, "end": v(-215.5, 22.5) * mm});
            skLineSegment(sketch, "E173.bottom", {"start": v(-81.5, 32.5) * mm, "end": v(-75.5, 32.5) * mm});
            skLineSegment(sketch, "E173.top", {"start": v(-81.5, 30.5) * mm, "end": v(-75.5, 30.5) * mm});
            skLineSegment(sketch, "E173.left", {"start": v(-81.5, 32.5) * mm, "end": v(-81.5, 30.5) * mm});
            skLineSegment(sketch, "E173.right", {"start": v(-75.5, 32.5) * mm, "end": v(-75.5, 30.5) * mm});
            skLineSegment(sketch, "E174.bottom", {"start": v(-81.5, 24.5) * mm, "end": v(-75.5, 24.5) * mm});
            skLineSegment(sketch, "E174.top", {"start": v(-81.5, 22.5) * mm, "end": v(-75.5, 22.5) * mm});
            skLineSegment(sketch, "E174.left", {"start": v(-81.5, 24.5) * mm, "end": v(-81.5, 22.5) * mm});
            skLineSegment(sketch, "E174.right", {"start": v(-75.5, 24.5) * mm, "end": v(-75.5, 22.5) * mm});
            skPoint(sketch, "E175", {"position": v(-208.5, 27.5) * mm});
            skLineSegment(sketch, "E176.bottom", {"start": v(198.5, 32.5) * mm, "end": v(204.5, 32.5) * mm});
            skLineSegment(sketch, "E176.top", {"start": v(198.5, 30.5) * mm, "end": v(204.5, 30.5) * mm});
            skLineSegment(sketch, "E176.left", {"start": v(198.5, 32.5) * mm, "end": v(198.5, 30.5) * mm});
            skLineSegment(sketch, "E176.right", {"start": v(204.5, 32.5) * mm, "end": v(204.5, 30.5) * mm});
            skLineSegment(sketch, "E177.bottom", {"start": v(198.5, 24.5) * mm, "end": v(204.5, 24.5) * mm});
            skLineSegment(sketch, "E177.top", {"start": v(198.5, 22.5) * mm, "end": v(204.5, 22.5) * mm});
            skLineSegment(sketch, "E177.left", {"start": v(198.5, 24.5) * mm, "end": v(198.5, 22.5) * mm});
            skLineSegment(sketch, "E177.right", {"start": v(204.5, 24.5) * mm, "end": v(204.5, 22.5) * mm});
            skLineSegment(sketch, "E178.bottom", {"start": v(58.5, 32.5) * mm, "end": v(64.5, 32.5) * mm});
            skLineSegment(sketch, "E178.top", {"start": v(58.5, 30.5) * mm, "end": v(64.5, 30.5) * mm});
            skLineSegment(sketch, "E178.left", {"start": v(58.5, 32.5) * mm, "end": v(58.5, 30.5) * mm});
            skLineSegment(sketch, "E178.right", {"start": v(64.5, 32.5) * mm, "end": v(64.5, 30.5) * mm});
            skLineSegment(sketch, "E179.bottom", {"start": v(58.5, 24.5) * mm, "end": v(64.5, 24.5) * mm});
            skLineSegment(sketch, "E179.top", {"start": v(58.5, 22.5) * mm, "end": v(64.5, 22.5) * mm});
            skLineSegment(sketch, "E179.left", {"start": v(58.5, 24.5) * mm, "end": v(58.5, 22.5) * mm});
            skLineSegment(sketch, "E179.right", {"start": v(64.5, 24.5) * mm, "end": v(64.5, 22.5) * mm});
            skPoint(sketch, "E180", {"position": v(-8.5, 18) * mm});
            skSolve(sketch);
        }
        {
            var Q0;
            Q0 = qSketchRegion(id + "F15", true);
            extrude(context, id + "F16", {"entities" : qUnion([Q0]), "depth" : 5 * mm});
        }
        {
            var Q0;
            Q0=makeQuery(id+"F10.opExtrude","CAP_FACE",FACE,{"disambiguationData":[OSD([sQuery(id+"F9.wireOp",EDGE,"E142.bottom"),sQuery(id+"F9.wireOp",EDGE,"E142.top"),sQuery(id+"F9.wireOp",EDGE,"E142.left"),sQuery(id+"F9.wireOp",EDGE,"E142.right"),sQuery(id+"F9.wireOp",EDGE,"E143.bottom"),sQuery(id+"F9.wireOp",EDGE,"E143.top"),sQuery(id+"F9.wireOp",EDGE,"E143.left"),sQuery(id+"F9.wireOp",EDGE,"E143.right"),sQuery(id+"F9.wireOp",EDGE,"E144"),sQuery(id+"F9.wireOp",EDGE,"E145"),sQuery(id+"F9.wireOp",EDGE,"E146.top"),sQuery(id+"F9.wireOp",EDGE,"E146.right"),sQuery(id+"F9.wireOp",EDGE,"E147.top"),sQuery(id+"F9.wireOp",EDGE,"E147.right"),sQuery(id+"F9.wireOp",EDGE,"E148.bottom"),sQuery(id+"F9.wireOp",EDGE,"E148.left"),sQuery(id+"F9.wireOp",EDGE,"E149.bottom"),sQuery(id+"F9.wireOp",EDGE,"E149.left")])],"isStart":false});
            var sketch = newSketch(context, id + "F17", { "sketchPlane" : qUnion([Q0])});
            skLineSegment(sketch, "E181.bottom", {"start": v(-295, 51) * mm, "end": v(-295, 213.5) * mm});
            skLineSegment(sketch, "E181.top", {"start": v(-127, 56.5) * mm, "end": v(-127, 219) * mm});
            skLineSegment(sketch, "E181.left", {"start": v(-289.5, 51) * mm, "end": v(-127, 51) * mm});
            skLineSegment(sketch, "E181.right", {"start": v(-295, 219) * mm, "end": v(-132.5, 219) * mm});
            skPoint(sketch, "E181.middle", {"position": v(-211, 135) * mm});
            skLineSegment(sketch, "E182", {"start": v(-295, 51) * mm, "end": v(-295, 47.5) * mm});
            skLineSegment(sketch, "E183", {"start": v(-295, 47.5) * mm, "end": v(-289.5, 47.5) * mm});
            skLineSegment(sketch, "E184", {"start": v(-289.5, 47.5) * mm, "end": v(-289.5, 51) * mm});
            skLineSegment(sketch, "E185", {"start": v(-127, 51) * mm, "end": v(-123.5, 51) * mm});
            skLineSegment(sketch, "E186", {"start": v(-123.5, 51) * mm, "end": v(-123.5, 56.5) * mm});
            skLineSegment(sketch, "E187", {"start": v(-123.5, 56.5) * mm, "end": v(-127, 56.5) * mm});
            skLineSegment(sketch, "E188", {"start": v(-127, 219) * mm, "end": v(-127, 222.5) * mm});
            skLineSegment(sketch, "E189", {"start": v(-127, 222.5) * mm, "end": v(-132.5, 222.5) * mm});
            skLineSegment(sketch, "E190", {"start": v(-132.5, 222.5) * mm, "end": v(-132.5, 219) * mm});
            skLineSegment(sketch, "E191", {"start": v(-295, 219) * mm, "end": v(-298.5, 219) * mm});
            skLineSegment(sketch, "E192", {"start": v(-298.5, 219) * mm, "end": v(-298.5, 213.5) * mm});
            skLineSegment(sketch, "E193", {"start": v(-298.5, 213.5) * mm, "end": v(-295, 213.5) * mm});
            skLineSegment(sketch, "E194.bottom", {"start": v(-306, -20) * mm, "end": v(-306, 290) * mm});
            skLineSegment(sketch, "E194.top", {"start": v(-116, 0) * mm, "end": v(-116, 290) * mm});
            skLineSegment(sketch, "E194.left", {"start": v(-306, -20) * mm, "end": v(-211, -20) * mm});
            skLineSegment(sketch, "E194.right", {"start": v(-306, 290) * mm, "end": v(-116, 290) * mm});
            skCircle(sketch, "E195", {"center": v(-131, 280) * mm, "radius": 2.25 * mm});
            skCircle(sketch, "E196", {"center": v(-291, -10) * mm, "radius": 2.25 * mm});
            skLineSegment(sketch, "E197", {"start": v(-211, -20) * mm, "end": v(-211, 0) * mm});
            skPoint(sketch, "E197.endSnap0", {"position": v(-211, -20) * mm});
            skLineSegment(sketch, "E198", {"start": v(-211, 0) * mm, "end": v(-116, 0) * mm});
            skPoint(sketch, "E199", {"position": v(-211, -10) * mm});
            skPoint(sketch, "E200.1.1", {"position": v(-211, -155) * mm});
            skLineSegment(sketch, "E200.1.2", {"start": v(-306, -20) * mm, "end": v(-306, -310) * mm});
            skLineSegment(sketch, "E200.1.3", {"start": v(-116, -310) * mm, "end": v(-306, -310) * mm});
            skLineSegment(sketch, "E200.1.4", {"start": v(-132.5, -71) * mm, "end": v(-295, -71) * mm});
            skLineSegment(sketch, "E200.1.5", {"start": v(-127, -239) * mm, "end": v(-289.5, -239) * mm});
            skLineSegment(sketch, "E200.1.6", {"start": v(-127, -71) * mm, "end": v(-127, -233.5) * mm});
            skLineSegment(sketch, "E200.1.7", {"start": v(-295, -76.5) * mm, "end": v(-295, -239) * mm});
            skLineSegment(sketch, "E200.1.8", {"start": v(-211, -20) * mm, "end": v(-306, -20) * mm});
            skLineSegment(sketch, "E200.1.9", {"start": v(-116, 0) * mm, "end": v(-211, 0) * mm});
            skPoint(sketch, "E200.1.10", {"position": v(-211, 0) * mm});
            skLineSegment(sketch, "E200.1.11", {"start": v(-116, 0) * mm, "end": v(-116, -310) * mm});
            skPoint(sketch, "E200.1.12", {"position": v(-211, -155) * mm});
            skCircle(sketch, "E200.1.13", {"center": v(-131, -10) * mm, "radius": 2.25 * mm});
            skLineSegment(sketch, "E200.1.14", {"start": v(-295, -71) * mm, "end": v(-298.5, -71) * mm});
            skLineSegment(sketch, "E200.1.15", {"start": v(-298.5, -71) * mm, "end": v(-298.5, -76.5) * mm});
            skLineSegment(sketch, "E200.1.16", {"start": v(-211, 0) * mm, "end": v(-211, -20) * mm});
            skLineSegment(sketch, "E200.1.17", {"start": v(-298.5, -76.5) * mm, "end": v(-295, -76.5) * mm});
            skCircle(sketch, "E200.1.18", {"center": v(-291, -300) * mm, "radius": 2.25 * mm});
            skLineSegment(sketch, "E200.1.19", {"start": v(-132.5, -67.5) * mm, "end": v(-132.5, -71) * mm});
            skLineSegment(sketch, "E200.1.20", {"start": v(-127, -67.5) * mm, "end": v(-132.5, -67.5) * mm});
            skLineSegment(sketch, "E200.1.21", {"start": v(-127, -239) * mm, "end": v(-123.5, -239) * mm});
            skLineSegment(sketch, "E200.1.22", {"start": v(-289.5, -242.5) * mm, "end": v(-289.5, -239) * mm});
            skLineSegment(sketch, "E200.1.23", {"start": v(-123.5, -233.5) * mm, "end": v(-127, -233.5) * mm});
            skLineSegment(sketch, "E200.1.24", {"start": v(-295, -239) * mm, "end": v(-295, -242.5) * mm});
            skLineSegment(sketch, "E200.1.25", {"start": v(-295, -242.5) * mm, "end": v(-289.5, -242.5) * mm});
            skLineSegment(sketch, "E200.1.26", {"start": v(-127, -71) * mm, "end": v(-127, -67.5) * mm});
            skLineSegment(sketch, "E200.1.27", {"start": v(-123.5, -239) * mm, "end": v(-123.5, -233.5) * mm});
            skSolve(sketch);
        }
        {
            var Q0;
            Q0 = qSketchRegion(id + "F17", true);
            extrude(context, id + "F18", {"entities" : qUnion([Q0]), "depth" : 5 * mm});
        }
    });
